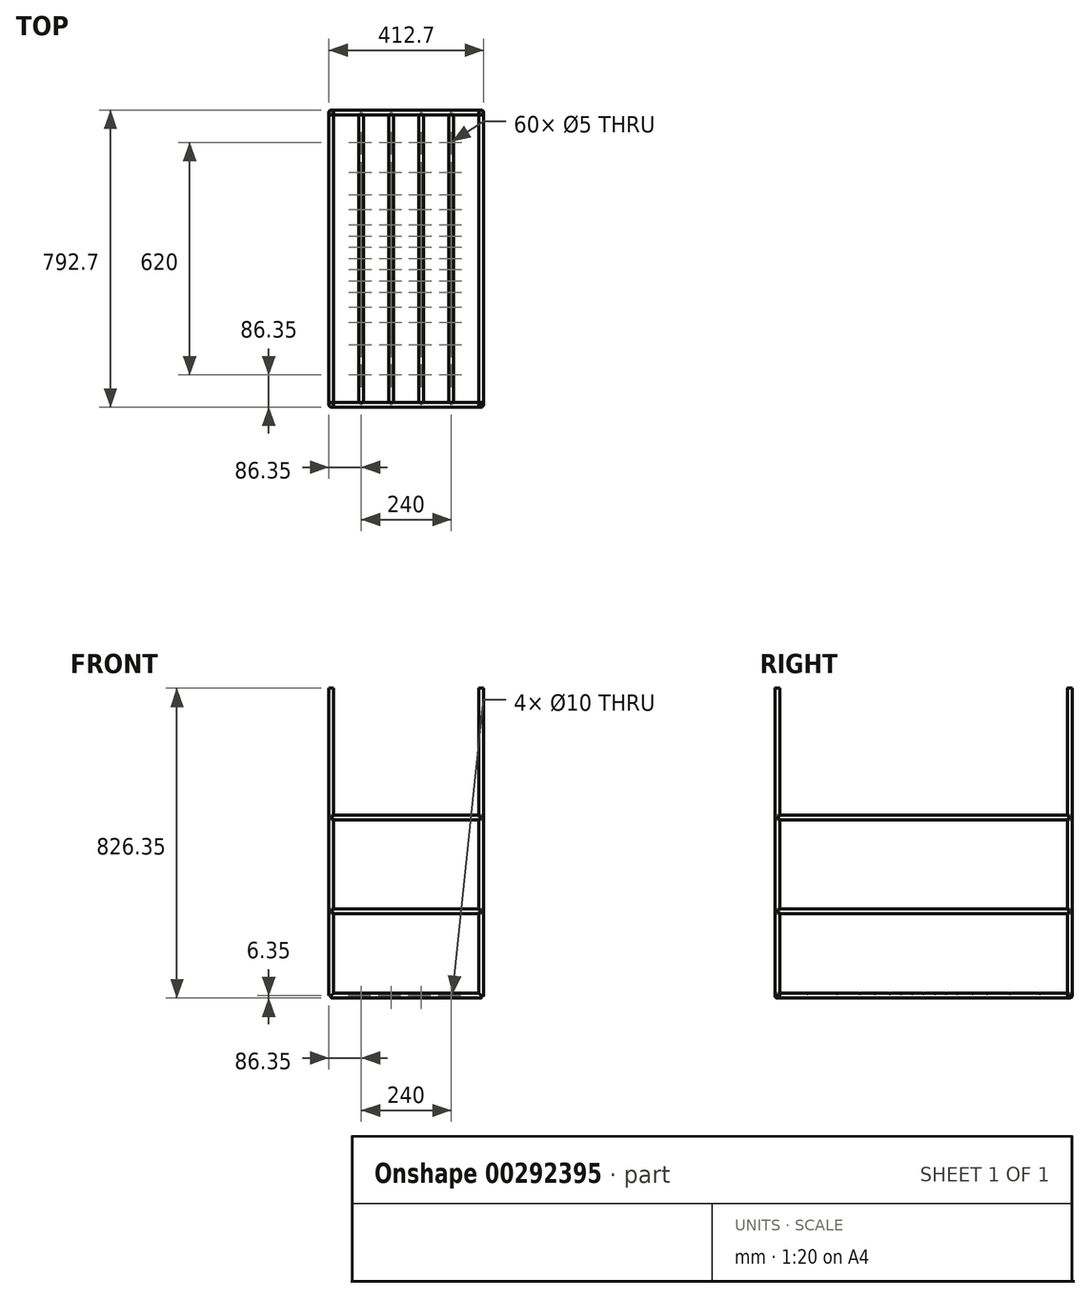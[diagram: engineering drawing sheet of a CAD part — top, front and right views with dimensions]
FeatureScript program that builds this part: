
annotation { "Feature Type Name" : "Feature", "Feature Type Description" : "" }
export const myFeature = defineFeature(function(context is Context, id is Id, definition is map)
    precondition{}
    {
        {
            var Q0;
            Q0=qCreatedBy(makeId("Right.planeOp"),FACE);
            var sketch = newSketch(context, id + "F0", { "sketchPlane" : qUnion([Q0])});
            skLineSegment(sketch, "E0", {"start": v(0, 0) * mm, "end": v(0, 225) * mm, "construction": true});
            skLineSegment(sketch, "E1", {"start": v(0, 225) * mm, "end": v(0, 475) * mm, "construction": true});
            skLineSegment(sketch, "E2", {"start": v(0, 475) * mm, "end": v(0, 820) * mm, "construction": true});
            skCircle(sketch, "E3", {"center": v(0, 0) * mm, "radius": 6.35 * mm});
            skCircle(sketch, "E4", {"center": v(0, 225) * mm, "radius": 6.35 * mm});
            skCircle(sketch, "E5", {"center": v(0, 475) * mm, "radius": 6.35 * mm});
            skCircle(sketch, "E6.1.0.0", {"center": v(780, 0) * mm, "radius": 6.35 * mm});
            skCircle(sketch, "E6.1.0.1", {"center": v(780, 225) * mm, "radius": 6.35 * mm});
            skCircle(sketch, "E6.1.0.2", {"center": v(780, 475) * mm, "radius": 6.35 * mm});
            skLineSegment(sketch, "E6.direction1", {"start": v(0, 0) * mm, "end": v(780, 0) * mm, "construction": true});
            skSolve(sketch);
        }
        {
            var Q0;
            Q0 = qSketchRegion(id + "F0", true);
            var Q1;
            Q1=sQuery(id+"F0.wireOp",EDGE,"E3");
            var Q2;
            Q2=sQuery(id+"F0.wireOp",EDGE,"E4");
            var Q3;
            Q3=sQuery(id+"F0.wireOp",EDGE,"E5");
            var Q4;
            Q4=sQuery(id+"F0.wireOp",EDGE,"E6.1.0.2");
            var Q5;
            Q5=sQuery(id+"F0.wireOp",EDGE,"E6.1.0.1");
            var Q6;
            Q6=sQuery(id+"F0.wireOp",EDGE,"E6.1.0.0");
            extrude(context, id + "F1", {"entities" : qUnion([Q0]), "surfaceEntities" : qUnion([Q1, Q2, Q3, Q4, Q5, Q6]), "oppositeDirection" : true, "depth" : 400 * mm});
        }
        {
            var Q0;
            Q0=qCreatedBy(makeId("Top.planeOp"),FACE);
            var sketch = newSketch(context, id + "F2", { "sketchPlane" : qUnion([Q0])});
            skCircle(sketch, "E7", {"center": v(0, 0) * mm, "radius": 6.35 * mm});
            skCircle(sketch, "E8.0.1.0", {"center": v(0, 780) * mm, "radius": 6.35 * mm});
            skCircle(sketch, "E8.1.0.0", {"center": v(-400, 0) * mm, "radius": 6.35 * mm});
            skCircle(sketch, "E8.1.1.0", {"center": v(-400, 780) * mm, "radius": 6.35 * mm});
            skLineSegment(sketch, "E8.direction1", {"start": v(0, 0) * mm, "end": v(-400, 0) * mm, "construction": true});
            skLineSegment(sketch, "E8.direction2", {"start": v(0, 0) * mm, "end": v(0, 780) * mm, "construction": true});
            skSolve(sketch);
        }
        {
            var Q0;
            Q0 = qSketchRegion(id + "F2", true);
            extrude(context, id + "F3", {"entities" : qUnion([Q0]), "operationType" : NewBodyOperationType.ADD, "depth" : 820 * mm});
        }
        {
            var Q0;
            Q0=qCreatedBy(makeId("Front.planeOp"),FACE);
            var sketch = newSketch(context, id + "F4", { "sketchPlane" : qUnion([Q0])});
            skLineSegment(sketch, "E9", {"start": v(0, 0) * mm, "end": v(0, 225) * mm});
            skLineSegment(sketch, "E10", {"start": v(0, 225) * mm, "end": v(0, 475) * mm});
            skLineSegment(sketch, "E11", {"start": v(0, 475) * mm, "end": v(0, 820) * mm});
            skCircle(sketch, "E12", {"center": v(0, 225) * mm, "radius": 6.35 * mm});
            skCircle(sketch, "E13", {"center": v(0, 475) * mm, "radius": 6.35 * mm});
            skCircle(sketch, "E14.1.0.1", {"center": v(-400, 225) * mm, "radius": 6.35 * mm});
            skCircle(sketch, "E14.1.0.2", {"center": v(-400, 475) * mm, "radius": 6.35 * mm});
            skLineSegment(sketch, "E14.direction1", {"start": v(0, 0) * mm, "end": v(-400, 0) * mm, "construction": true});
            skLineSegment(sketch, "E15", {"start": v(0, 0) * mm, "end": v(-80, 0) * mm});
            skCircle(sketch, "E16", {"center": v(-80, 0) * mm, "radius": 6.35 * mm});
            skCircle(sketch, "E17.1.0.0", {"center": v(-160, 0) * mm, "radius": 6.35 * mm});
            skCircle(sketch, "E17.2.0.0", {"center": v(-240, 0) * mm, "radius": 6.35 * mm});
            skCircle(sketch, "E17.3.0.0", {"center": v(-320, 0) * mm, "radius": 6.35 * mm});
            skLineSegment(sketch, "E17.direction1", {"start": v(-80, 0) * mm, "end": v(-160, 0) * mm, "construction": true});
            skCircle(sketch, "E18", {"center": v(-80, 0) * mm, "radius": 5 * mm});
            skCircle(sketch, "E19.1.0.0", {"center": v(-160, 0) * mm, "radius": 5 * mm});
            skCircle(sketch, "E19.2.0.0", {"center": v(-240, 0) * mm, "radius": 5 * mm});
            skCircle(sketch, "E19.3.0.0", {"center": v(-320, 0) * mm, "radius": 5 * mm});
            skSolve(sketch);
        }
        {
            var Q0;
            Q0 = qSketchRegion(id + "F4", true);
            extrude(context, id + "F5", {"entities" : qUnion([Q0]), "operationType" : NewBodyOperationType.ADD, "oppositeDirection" : true, "depth" : 780 * mm});
        }
        {
            var Q0;
            Q0=qCreatedBy(makeId("Top.planeOp"),FACE);
            var sketch = newSketch(context, id + "F6", { "sketchPlane" : qUnion([Q0])});
            skLineSegment(sketch, "E20", {"start": v(0, 0) * mm, "end": v(-80, 0) * mm, "construction": true});
            skLineSegment(sketch, "E21", {"start": v(-80, 0) * mm, "end": v(-80, 390) * mm, "construction": true});
            skLineSegment(sketch, "E22", {"start": v(-80, 0) * mm, "end": v(-80, 80) * mm, "construction": true});
            skLineSegment(sketch, "E23", {"start": v(-80, 80) * mm, "end": v(-80, 160) * mm, "construction": true});
            skLineSegment(sketch, "E24", {"start": v(-80, 160) * mm, "end": v(-80, 220) * mm, "construction": true});
            skLineSegment(sketch, "E25", {"start": v(-80, 220) * mm, "end": v(-80, 260) * mm, "construction": true});
            skLineSegment(sketch, "E26", {"start": v(-80, 260) * mm, "end": v(-80, 300) * mm, "construction": true});
            skLineSegment(sketch, "E27", {"start": v(-80, 300) * mm, "end": v(-80, 330) * mm, "construction": true});
            skLineSegment(sketch, "E28", {"start": v(-80, 330) * mm, "end": v(-80, 360) * mm, "construction": true});
            skCircle(sketch, "E29", {"center": v(-80, 80) * mm, "radius": 2.5 * mm});
            skCircle(sketch, "E30", {"center": v(-80, 160) * mm, "radius": 2.5 * mm});
            skCircle(sketch, "E31", {"center": v(-80, 220) * mm, "radius": 2.5 * mm});
            skCircle(sketch, "E32", {"center": v(-80, 300) * mm, "radius": 2.5 * mm});
            skCircle(sketch, "E33", {"center": v(-80, 260) * mm, "radius": 2.5 * mm});
            skCircle(sketch, "E34", {"center": v(-80, 330) * mm, "radius": 2.5 * mm});
            skCircle(sketch, "E35", {"center": v(-80, 360) * mm, "radius": 2.5 * mm});
            skLineSegment(sketch, "E36", {"start": v(-80, 390) * mm, "end": v(25.48, 390) * mm, "construction": true});
            skCircle(sketch, "E37.MirrorC", {"center": v(-80, 420) * mm, "radius": 2.5 * mm});
            skCircle(sketch, "E38.MirrorC", {"center": v(-80, 450) * mm, "radius": 2.5 * mm});
            skCircle(sketch, "E39.MirrorC", {"center": v(-80, 480) * mm, "radius": 2.5 * mm});
            skCircle(sketch, "E40.MirrorC", {"center": v(-80, 520) * mm, "radius": 2.5 * mm});
            skCircle(sketch, "E41.MirrorC", {"center": v(-80, 560) * mm, "radius": 2.5 * mm});
            skCircle(sketch, "E42.MirrorC", {"center": v(-80, 620) * mm, "radius": 2.5 * mm});
            skCircle(sketch, "E43.MirrorC", {"center": v(-80, 700) * mm, "radius": 2.5 * mm});
            skCircle(sketch, "E44", {"center": v(-80, 390) * mm, "radius": 2.5 * mm});
            skCircle(sketch, "E45.1.0.0", {"center": v(-160, 560) * mm, "radius": 2.5 * mm});
            skCircle(sketch, "E45.1.0.1", {"center": v(-160, 700) * mm, "radius": 2.5 * mm});
            skCircle(sketch, "E45.1.0.2", {"center": v(-160, 620) * mm, "radius": 2.5 * mm});
            skCircle(sketch, "E45.1.0.3", {"center": v(-160, 520) * mm, "radius": 2.5 * mm});
            skCircle(sketch, "E45.1.0.4", {"center": v(-160, 420) * mm, "radius": 2.5 * mm});
            skCircle(sketch, "E45.1.0.5", {"center": v(-160, 480) * mm, "radius": 2.5 * mm});
            skCircle(sketch, "E45.1.0.6", {"center": v(-160, 450) * mm, "radius": 2.5 * mm});
            skCircle(sketch, "E45.1.0.7", {"center": v(-160, 220) * mm, "radius": 2.5 * mm});
            skCircle(sketch, "E45.1.0.8", {"center": v(-160, 390) * mm, "radius": 2.5 * mm});
            skCircle(sketch, "E45.1.0.9", {"center": v(-160, 80) * mm, "radius": 2.5 * mm});
            skCircle(sketch, "E45.1.0.10", {"center": v(-160, 330) * mm, "radius": 2.5 * mm});
            skCircle(sketch, "E45.1.0.11", {"center": v(-160, 160) * mm, "radius": 2.5 * mm});
            skCircle(sketch, "E45.1.0.12", {"center": v(-160, 360) * mm, "radius": 2.5 * mm});
            skCircle(sketch, "E45.1.0.13", {"center": v(-160, 260) * mm, "radius": 2.5 * mm});
            skCircle(sketch, "E45.1.0.14", {"center": v(-160, 300) * mm, "radius": 2.5 * mm});
            skCircle(sketch, "E45.2.0.0", {"center": v(-240, 560) * mm, "radius": 2.5 * mm});
            skCircle(sketch, "E45.2.0.1", {"center": v(-240, 700) * mm, "radius": 2.5 * mm});
            skCircle(sketch, "E45.2.0.2", {"center": v(-240, 620) * mm, "radius": 2.5 * mm});
            skCircle(sketch, "E45.2.0.3", {"center": v(-240, 520) * mm, "radius": 2.5 * mm});
            skCircle(sketch, "E45.2.0.4", {"center": v(-240, 420) * mm, "radius": 2.5 * mm});
            skCircle(sketch, "E45.2.0.5", {"center": v(-240, 480) * mm, "radius": 2.5 * mm});
            skCircle(sketch, "E45.2.0.6", {"center": v(-240, 450) * mm, "radius": 2.5 * mm});
            skCircle(sketch, "E45.2.0.7", {"center": v(-240, 220) * mm, "radius": 2.5 * mm});
            skCircle(sketch, "E45.2.0.8", {"center": v(-240, 390) * mm, "radius": 2.5 * mm});
            skCircle(sketch, "E45.2.0.9", {"center": v(-240, 80) * mm, "radius": 2.5 * mm});
            skCircle(sketch, "E45.2.0.10", {"center": v(-240, 330) * mm, "radius": 2.5 * mm});
            skCircle(sketch, "E45.2.0.11", {"center": v(-240, 160) * mm, "radius": 2.5 * mm});
            skCircle(sketch, "E45.2.0.12", {"center": v(-240, 360) * mm, "radius": 2.5 * mm});
            skCircle(sketch, "E45.2.0.13", {"center": v(-240, 260) * mm, "radius": 2.5 * mm});
            skCircle(sketch, "E45.2.0.14", {"center": v(-240, 300) * mm, "radius": 2.5 * mm});
            skCircle(sketch, "E45.3.0.0", {"center": v(-320, 560) * mm, "radius": 2.5 * mm});
            skCircle(sketch, "E45.3.0.1", {"center": v(-320, 700) * mm, "radius": 2.5 * mm});
            skCircle(sketch, "E45.3.0.2", {"center": v(-320, 620) * mm, "radius": 2.5 * mm});
            skCircle(sketch, "E45.3.0.3", {"center": v(-320, 520) * mm, "radius": 2.5 * mm});
            skCircle(sketch, "E45.3.0.4", {"center": v(-320, 420) * mm, "radius": 2.5 * mm});
            skCircle(sketch, "E45.3.0.5", {"center": v(-320, 480) * mm, "radius": 2.5 * mm});
            skCircle(sketch, "E45.3.0.6", {"center": v(-320, 450) * mm, "radius": 2.5 * mm});
            skCircle(sketch, "E45.3.0.7", {"center": v(-320, 220) * mm, "radius": 2.5 * mm});
            skCircle(sketch, "E45.3.0.8", {"center": v(-320, 390) * mm, "radius": 2.5 * mm});
            skCircle(sketch, "E45.3.0.9", {"center": v(-320, 80) * mm, "radius": 2.5 * mm});
            skCircle(sketch, "E45.3.0.10", {"center": v(-320, 330) * mm, "radius": 2.5 * mm});
            skCircle(sketch, "E45.3.0.11", {"center": v(-320, 160) * mm, "radius": 2.5 * mm});
            skCircle(sketch, "E45.3.0.12", {"center": v(-320, 360) * mm, "radius": 2.5 * mm});
            skCircle(sketch, "E45.3.0.13", {"center": v(-320, 260) * mm, "radius": 2.5 * mm});
            skCircle(sketch, "E45.3.0.14", {"center": v(-320, 300) * mm, "radius": 2.5 * mm});
            skLineSegment(sketch, "E45.direction1", {"start": v(-80, 80) * mm, "end": v(-160, 80) * mm, "construction": true});
            skSolve(sketch);
        }
        {
            var Q0;
            Q0 = qSketchRegion(id + "F6", true);
            extrude(context, id + "F7", {"entities" : qUnion([Q0]), "operationType" : NewBodyOperationType.REMOVE, "depth" : 25 * mm});
        }
    });
